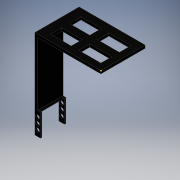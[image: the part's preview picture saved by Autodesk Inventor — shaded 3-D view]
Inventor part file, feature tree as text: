
AUTODESK INVENTOR PART (.ipt)
format: ipt  version: 2016 (Build 200138000, 138)  size: 175,616 bytes
history: native  units: mm
features: sketch x7, extrude x5, hole x1
ambient origin geometry x8: Origin, YZ Plane, XZ Plane, XY Plane, X Axis, Y Axis, Z Axis, Center Point
bodies: Body1 (feature_tree)
feature tree (13):
  extrude  "Extrusion2"  Depth=70.0mm
  extrude  "Extrusion3"  Depth=27.0mm TaperAngle=0.0deg
  extrude  "Extrusion4"  Depth=24.0mm
  extrude  "Extrusion5"  Depth=1.5mm
  extrude  "Extrusion6"  Depth=53.0mm
  sketch  "Sketch11"  dims[d46=32.0mm d47=7.0mm]
  hole  "Hole2"  [1 undecoded]
  sketch  "Sketch3"  dims[d26=70.0mm d27=70.0mm]
  sketch  "Sketch4"  dims[d29=6.0mm d31=27.0mm d32=0.0mm]
  sketch  "Sketch5"  dims[d34=20.0mm d35=0.0mm d36=24.0mm]
  sketch  "Sketch9"  dims[d37=24.0mm d38=1.5mm]
  sketch  "Sketch10"  dims[d39=10.0mm d40=0.0mm d45=53.0mm]
  sketch  "Sketch12"  dims[d48=7.0mm d49=10.0mm d50=0.0mm d51=8.0mm d52=8.0mm d53=3.0mm d54=0.0mm d55=4.25mm d56=4.25mm d57=4.25mm d59=6.0mm d60=6.0mm d61=6.0mm d62=4.25mm d63=4.25mm d64=4.25mm d65=6.0mm d66=6.0mm d67=6.0mm d68=4.25mm d69=6.0mm d70=4.0mm d71=2.0mm d72=90.0deg d73=8.0mm d74=0.0mm]
note: 1 required parameter value undecoded (feature->parameter linkage not recoverable at this tier; creation-order binding heuristic only, values carry confidence <= 0.55)
